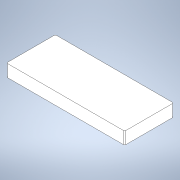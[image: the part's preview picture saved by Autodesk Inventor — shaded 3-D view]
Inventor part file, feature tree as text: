
AUTODESK INVENTOR PART (.ipt)
format: ipt  version: 2022 (Build 260153000, 153)  size: 105,472 bytes
history: native  units: in
note: dims shown in document units (in); Inventor stores cm internally (conversion verified against a paired STEP export)
features: fillet x4, extrude x1, sketch x1
ambient origin geometry x8: Origin, YZ Plane, XZ Plane, XY Plane, X Axis, Y Axis, Z Axis, Center Point
bodies: Solid1 (feature_tree)
feature tree (6):
  extrude  "Extrusion1"  Depth=4.7244in
  fillet  "Face Fillet1"
  fillet  "Face Fillet2"
  fillet  "Face Fillet3"
  fillet  "Face Fillet4"
  sketch  "Sketch1"  dims[d0=11.4173in d1=4.7244in d2=1.1811in d3=0.0in d4=0.1181in d5=0.1181in d6=0.1181in d7=0.1181in]
